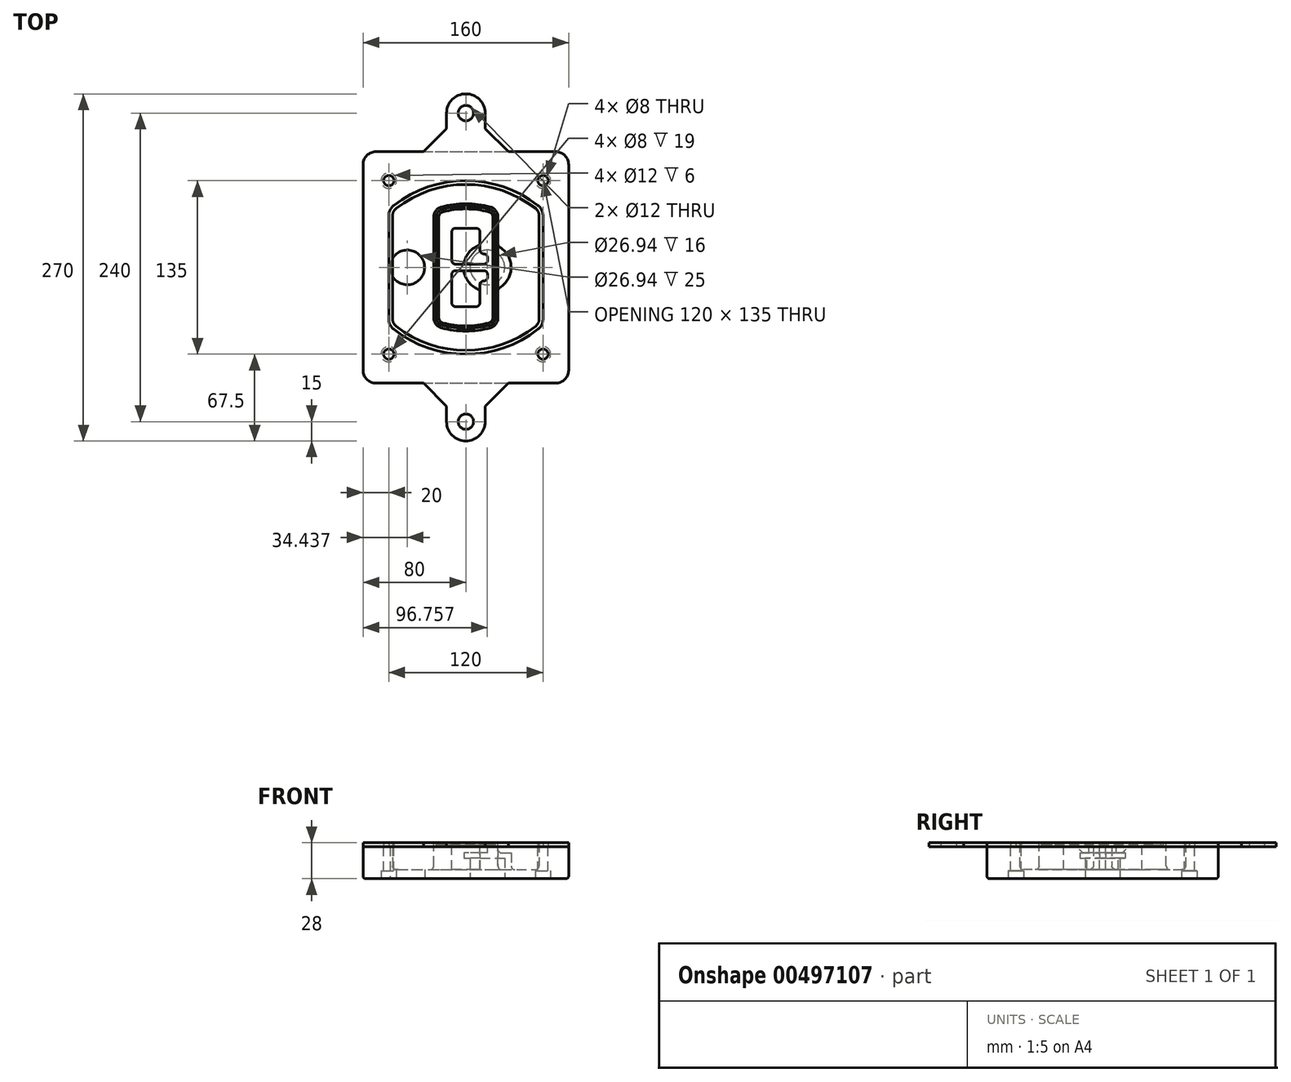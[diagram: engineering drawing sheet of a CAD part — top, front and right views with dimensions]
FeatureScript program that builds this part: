
annotation { "Feature Type Name" : "Feature", "Feature Type Description" : "" }
export const myFeature = defineFeature(function(context is Context, id is Id, definition is map)
    precondition{}
    {
        {
            var Q0;
            Q0=qCreatedBy(makeId("Top.planeOp"),FACE);
            var sketch = newSketch(context, id + "F0", { "sketchPlane" : qUnion([Q0])});
            skPoint(sketch, "E0.rect.middle", {"position": v(0, 0) * mm});
            skLineSegment(sketch, "E1.bottom", {"start": v(-70, -90) * mm, "end": v(70, -90) * mm});
            skLineSegment(sketch, "E1.top", {"start": v(-70, 90) * mm, "end": v(70, 90) * mm});
            skLineSegment(sketch, "E1.left", {"start": v(-80, -80) * mm, "end": v(-80, 80) * mm});
            skLineSegment(sketch, "E1.right", {"start": v(80, -80) * mm, "end": v(80, 80) * mm});
            skLineSegment(sketch, "E2", {"start": v(-80, 90) * mm, "end": v(80, -90) * mm, "construction": true});
            skLineSegment(sketch, "E3", {"start": v(80, 90) * mm, "end": v(-80, -90) * mm, "construction": true});
            skCircle(sketch, "E4", {"center": v(-60, 67.5) * mm, "radius": 4 * mm});
            skCircle(sketch, "E5", {"center": v(60, 67.5) * mm, "radius": 4 * mm});
            skCircle(sketch, "E6", {"center": v(60, -67.5) * mm, "radius": 4 * mm});
            skCircle(sketch, "E7", {"center": v(-60, -67.5) * mm, "radius": 4 * mm});
            skLineSegment(sketch, "E8", {"start": v(-60, 67.5) * mm, "end": v(60, 67.5) * mm, "construction": true});
            skLineSegment(sketch, "E9", {"start": v(60, 67.5) * mm, "end": v(60, -67.5) * mm, "construction": true});
            skLineSegment(sketch, "E10", {"start": v(60, -67.5) * mm, "end": v(-60, -67.5) * mm, "construction": true});
            skLineSegment(sketch, "E11", {"start": v(-60, -67.5) * mm, "end": v(-60, 67.5) * mm, "construction": true});
            skLineSegment(sketch, "E12", {"start": v(-60, 40.3) * mm, "end": v(-60, -40.3) * mm});
            skLineSegment(sketch, "E13", {"start": v(60, 40.3) * mm, "end": v(60, -40.3) * mm});
            skArc(sketch, "E14", {"start": v(56.15, 48.18) * mm, "mid": v(0, 67.5) * mm, "end": v(-56.15, 48.18) * mm});
            skArc(sketch, "E15", {"start": v(-56.15, -48.18) * mm, "mid": v(0, -67.5) * mm, "end": v(56.15, -48.18) * mm});
            skLineSegment(sketch, "E16", {"start": v(-60, 0) * mm, "end": v(60, 0) * mm, "construction": true});
            skPoint(sketch, "E17.visualSharp", {"position": v(-60, -45) * mm});
            skArc(sketch, "E17.filletArc", {"start": v(-60, -40.3) * mm, "mid": v(-58.99, -44.68) * mm, "end": v(-56.15, -48.18) * mm});
            skPoint(sketch, "E18.visualSharp", {"position": v(-60, 45) * mm});
            skArc(sketch, "E18.filletArc", {"start": v(-56.15, 48.18) * mm, "mid": v(-58.99, 44.68) * mm, "end": v(-60, 40.3) * mm});
            skPoint(sketch, "E19.visualSharp", {"position": v(60, 45) * mm});
            skArc(sketch, "E19.filletArc", {"start": v(60, 40.3) * mm, "mid": v(58.99, 44.68) * mm, "end": v(56.15, 48.18) * mm});
            skPoint(sketch, "E20.visualSharp", {"position": v(60, -45) * mm});
            skArc(sketch, "E20.filletArc", {"start": v(56.15, -48.18) * mm, "mid": v(58.99, -44.68) * mm, "end": v(60, -40.3) * mm});
            skPoint(sketch, "E21.visualSharp", {"position": v(-80, 90) * mm});
            skArc(sketch, "E21.filletArc", {"start": v(-70, 90) * mm, "mid": v(-77.07, 87.07) * mm, "end": v(-80, 80) * mm});
            skPoint(sketch, "E22.visualSharp", {"position": v(80, 90) * mm});
            skArc(sketch, "E22.filletArc", {"start": v(80, 80) * mm, "mid": v(77.07, 87.07) * mm, "end": v(70, 90) * mm});
            skPoint(sketch, "E23.visualSharp", {"position": v(80, -90) * mm});
            skArc(sketch, "E23.filletArc", {"start": v(70, -90) * mm, "mid": v(77.07, -87.07) * mm, "end": v(80, -80) * mm});
            skPoint(sketch, "E24.visualSharp", {"position": v(-80, -90) * mm});
            skArc(sketch, "E24.filletArc", {"start": v(-80, -80) * mm, "mid": v(-77.07, -87.07) * mm, "end": v(-70, -90) * mm});
            skArc(sketch, "E25.0", {"start": v(57, 40.3) * mm, "mid": v(56.3, 43.36) * mm, "end": v(54.3, 45.81) * mm});
            skLineSegment(sketch, "E25.1", {"start": v(57, 40.3) * mm, "end": v(57, -40.3) * mm});
            skArc(sketch, "E25.2", {"start": v(54.3, -45.81) * mm, "mid": v(56.3, -43.36) * mm, "end": v(57, -40.3) * mm});
            skArc(sketch, "E25.3", {"start": v(-54.3, -45.81) * mm, "mid": v(0, -64.5) * mm, "end": v(54.3, -45.81) * mm});
            skArc(sketch, "E25.4", {"start": v(-57, -40.3) * mm, "mid": v(-56.3, -43.36) * mm, "end": v(-54.3, -45.81) * mm});
            skArc(sketch, "E25.5", {"start": v(54.3, 45.81) * mm, "mid": v(0, 64.5) * mm, "end": v(-54.3, 45.81) * mm});
            skLineSegment(sketch, "E25.6", {"start": v(-57, 40.3) * mm, "end": v(-57, -40.3) * mm});
            skArc(sketch, "E25.7", {"start": v(-54.3, 45.81) * mm, "mid": v(-56.3, 43.36) * mm, "end": v(-57, 40.3) * mm});
            skArc(sketch, "E26.0", {"start": v(-58.62, 51.33) * mm, "mid": v(-62.58, 46.43) * mm, "end": v(-64, 40.3) * mm});
            skArc(sketch, "E26.1", {"start": v(58.62, 51.33) * mm, "mid": v(0, 71.5) * mm, "end": v(-58.62, 51.33) * mm});
            skArc(sketch, "E26.2", {"start": v(64, 40.3) * mm, "mid": v(62.58, 46.43) * mm, "end": v(58.62, 51.33) * mm});
            skLineSegment(sketch, "E26.3", {"start": v(64, 40.3) * mm, "end": v(64, -40.3) * mm});
            skArc(sketch, "E26.4", {"start": v(58.62, -51.33) * mm, "mid": v(62.58, -46.43) * mm, "end": v(64, -40.3) * mm});
            skLineSegment(sketch, "E26.5", {"start": v(-64, 40.3) * mm, "end": v(-64, -40.3) * mm});
            skArc(sketch, "E26.6", {"start": v(-58.62, -51.33) * mm, "mid": v(0, -71.5) * mm, "end": v(58.62, -51.33) * mm});
            skArc(sketch, "E26.7", {"start": v(-64, -40.3) * mm, "mid": v(-62.58, -46.43) * mm, "end": v(-58.62, -51.33) * mm});
            skSolve(sketch);
        }
        {
            var Q0;
            Q0=makeQuery(id+"F0.imprint","IMPRINT",FACE,{"disambiguationData":[TD([[makeQuery(id+"F0.imprint","IMPRINT",EDGE,{"derivedFrom":sQuery(id+"F0.wireOp",EDGE,"E1.bottom")}),1.0]])]});
            var Q1;
            Q1=makeQuery(id+"F0.imprint","IMPRINT",FACE,{"disambiguationData":[TD([[makeQuery(id+"F0.imprint","IMPRINT",EDGE,{"derivedFrom":sQuery(id+"F0.wireOp",EDGE,"E12")}),1.0]])]});
            var Q2;
            Q2=makeQuery(id+"F0.imprint","IMPRINT",FACE,{"disambiguationData":[TD([[makeQuery(id+"F0.imprint","IMPRINT",EDGE,{"derivedFrom":sQuery(id+"F0.wireOp",EDGE,"E25.0")}),1.0]])]});
            var Q3;
            Q3=makeQuery(id+"F0.imprint","IMPRINT",FACE,{"disambiguationData":[TD([[makeQuery(id+"F0.imprint","IMPRINT",EDGE,{"derivedFrom":sQuery(id+"F0.wireOp",EDGE,"E12")}),-1.0]])]});
            extrude(context, id + "F1", {"entities" : qUnion([Q0, Q1, Q2, Q3]), "oppositeDirection" : true, "depth" : 25 * mm});
        }
        {
            var Q0;
            Q0=makeQuery(id+"F0.imprint","IMPRINT",FACE,{"disambiguationData":[TD([[makeQuery(id+"F0.imprint","IMPRINT",EDGE,{"derivedFrom":sQuery(id+"F0.wireOp",EDGE,"E12")}),1.0]])]});
            extrude(context, id + "F2", {"entities" : qUnion([Q0]), "operationType" : NewBodyOperationType.ADD, "depth" : 3 * mm});
        }
        {
            var Q0;
            Q0=makeQuery(id+"F0.imprint","IMPRINT",FACE,{"disambiguationData":[TD([[makeQuery(id+"F0.imprint","IMPRINT",EDGE,{"derivedFrom":sQuery(id+"F0.wireOp",EDGE,"E25.0")}),1.0]])]});
            extrude(context, id + "F3", {"entities" : qUnion([Q0]), "operationType" : NewBodyOperationType.REMOVE, "oppositeDirection" : true, "depth" : 18 * mm});
        }
        {
            var Q0;
            Q0=makeQuery(id+"F2.opExtrude","CAP_FACE",FACE,{"disambiguationData":[OSD([sQuery(id+"F0.wireOp",EDGE,"E12"),sQuery(id+"F0.wireOp",EDGE,"E13"),sQuery(id+"F0.wireOp",EDGE,"E14"),sQuery(id+"F0.wireOp",EDGE,"E15"),sQuery(id+"F0.wireOp",EDGE,"E17.filletArc"),sQuery(id+"F0.wireOp",EDGE,"E18.filletArc"),sQuery(id+"F0.wireOp",EDGE,"E19.filletArc"),sQuery(id+"F0.wireOp",EDGE,"E20.filletArc"),sQuery(id+"F0.wireOp",EDGE,"E25.0"),sQuery(id+"F0.wireOp",EDGE,"E25.1"),sQuery(id+"F0.wireOp",EDGE,"E25.2"),sQuery(id+"F0.wireOp",EDGE,"E25.3"),sQuery(id+"F0.wireOp",EDGE,"E25.4"),sQuery(id+"F0.wireOp",EDGE,"E25.5"),sQuery(id+"F0.wireOp",EDGE,"E25.6"),sQuery(id+"F0.wireOp",EDGE,"E25.7")])],"isStart":false});
            var sketch = newSketch(context, id + "F4", { "sketchPlane" : qUnion([Q0])});
            skArc(sketch, "E27.0", {"start": v(-19.08, -46.97) * mm, "mid": v(0, -49.5) * mm, "end": v(19.08, -46.97) * mm});
            skArc(sketch, "E28.0", {"start": v(19.08, 46.97) * mm, "mid": v(0, 49.5) * mm, "end": v(-19.08, 46.97) * mm});
            skLineSegment(sketch, "E29", {"start": v(-25, 39.25) * mm, "end": v(-25, -39.25) * mm});
            skLineSegment(sketch, "E30", {"start": v(25, 39.25) * mm, "end": v(25, -39.25) * mm});
            skLineSegment(sketch, "E31", {"start": v(-25, 45.1) * mm, "end": v(25, 45.1) * mm, "construction": true});
            skLineSegment(sketch, "E32", {"start": v(-25, -45.1) * mm, "end": v(25, -45.1) * mm, "construction": true});
            skPoint(sketch, "E33.visualSharp", {"position": v(-25, 45.1) * mm});
            skArc(sketch, "E33.filletArc", {"start": v(-19.08, 46.97) * mm, "mid": v(-23.35, 44.11) * mm, "end": v(-25, 39.25) * mm});
            skPoint(sketch, "E34.visualSharp", {"position": v(25, 45.1) * mm});
            skArc(sketch, "E34.filletArc", {"start": v(25, 39.25) * mm, "mid": v(23.35, 44.11) * mm, "end": v(19.08, 46.97) * mm});
            skPoint(sketch, "E35.visualSharp", {"position": v(25, -45.1) * mm});
            skArc(sketch, "E35.filletArc", {"start": v(19.08, -46.97) * mm, "mid": v(23.35, -44.11) * mm, "end": v(25, -39.25) * mm});
            skPoint(sketch, "E36.visualSharp", {"position": v(-25, -45.1) * mm});
            skArc(sketch, "E36.filletArc", {"start": v(-25, -39.25) * mm, "mid": v(-23.35, -44.11) * mm, "end": v(-19.08, -46.97) * mm});
            skArc(sketch, "E37.0", {"start": v(54.3, 45.81) * mm, "mid": v(0, 64.5) * mm, "end": v(-54.3, 45.81) * mm});
            skArc(sketch, "E37.1", {"start": v(-54.3, 45.81) * mm, "mid": v(-56.3, 43.36) * mm, "end": v(-57, 40.3) * mm});
            skLineSegment(sketch, "E37.2", {"start": v(-57, 40.3) * mm, "end": v(-57, -40.3) * mm});
            skArc(sketch, "E37.3", {"start": v(-57, -40.3) * mm, "mid": v(-56.3, -43.36) * mm, "end": v(-54.3, -45.81) * mm});
            skArc(sketch, "E37.4", {"start": v(-54.3, -45.81) * mm, "mid": v(0, -64.5) * mm, "end": v(54.3, -45.81) * mm});
            skArc(sketch, "E37.5", {"start": v(54.3, -45.81) * mm, "mid": v(56.3, -43.36) * mm, "end": v(57, -40.3) * mm});
            skLineSegment(sketch, "E37.6", {"start": v(57, 40.3) * mm, "end": v(57, -40.3) * mm});
            skArc(sketch, "E37.7", {"start": v(57, 40.3) * mm, "mid": v(56.3, 43.36) * mm, "end": v(54.3, 45.81) * mm});
            skLineSegment(sketch, "E38.0", {"start": v(23, 39.25) * mm, "end": v(23, -39.25) * mm});
            skArc(sketch, "E38.1", {"start": v(18.56, -45.04) * mm, "mid": v(21.76, -42.9) * mm, "end": v(23, -39.25) * mm});
            skArc(sketch, "E38.2", {"start": v(-18.56, -45.04) * mm, "mid": v(0, -47.5) * mm, "end": v(18.56, -45.04) * mm});
            skArc(sketch, "E38.3", {"start": v(-23, -39.25) * mm, "mid": v(-21.76, -42.9) * mm, "end": v(-18.56, -45.04) * mm});
            skLineSegment(sketch, "E38.4", {"start": v(-23, 39.25) * mm, "end": v(-23, -39.25) * mm});
            skArc(sketch, "E38.5", {"start": v(23, 39.25) * mm, "mid": v(21.76, 42.9) * mm, "end": v(18.56, 45.04) * mm});
            skArc(sketch, "E38.6", {"start": v(-18.56, 45.04) * mm, "mid": v(-21.76, 42.9) * mm, "end": v(-23, 39.25) * mm});
            skArc(sketch, "E38.7", {"start": v(18.56, 45.04) * mm, "mid": v(0, 47.5) * mm, "end": v(-18.56, 45.04) * mm});
            skArc(sketch, "E39.0", {"start": v(21, 39.25) * mm, "mid": v(20.18, 41.68) * mm, "end": v(18.04, 43.1) * mm});
            skLineSegment(sketch, "E39.1", {"start": v(21, 39.25) * mm, "end": v(21, -39.25) * mm});
            skArc(sketch, "E39.2", {"start": v(18.04, -43.1) * mm, "mid": v(20.18, -41.68) * mm, "end": v(21, -39.25) * mm});
            skArc(sketch, "E39.3", {"start": v(-18.04, -43.1) * mm, "mid": v(0, -45.5) * mm, "end": v(18.04, -43.1) * mm});
            skArc(sketch, "E39.4", {"start": v(-21, -39.25) * mm, "mid": v(-20.18, -41.68) * mm, "end": v(-18.04, -43.1) * mm});
            skArc(sketch, "E39.5", {"start": v(18.04, 43.1) * mm, "mid": v(0, 45.5) * mm, "end": v(-18.04, 43.1) * mm});
            skLineSegment(sketch, "E39.6", {"start": v(-21, 39.25) * mm, "end": v(-21, -39.25) * mm});
            skArc(sketch, "E39.7", {"start": v(-18.04, 43.1) * mm, "mid": v(-20.18, 41.68) * mm, "end": v(-21, 39.25) * mm});
            skLineSegment(sketch, "E40", {"start": v(-25, 0) * mm, "end": v(25, 0) * mm, "construction": true});
            skLineSegment(sketch, "E41", {"start": v(-11, 5.5) * mm, "end": v(-11, 27.5) * mm});
            skLineSegment(sketch, "E42", {"start": v(-8, 30.5) * mm, "end": v(8, 30.5) * mm});
            skLineSegment(sketch, "E43", {"start": v(11, 27.5) * mm, "end": v(11, 13.5) * mm});
            skLineSegment(sketch, "E44", {"start": v(14, 10.5) * mm, "end": v(14, 10.5) * mm});
            skLineSegment(sketch, "E45", {"start": v(17, 7.5) * mm, "end": v(17, 5.5) * mm});
            skLineSegment(sketch, "E46", {"start": v(14, 2.5) * mm, "end": v(-8, 2.5) * mm});
            skPoint(sketch, "E47.visualSharp", {"position": v(-11, 30.5) * mm});
            skArc(sketch, "E47.filletArc", {"start": v(-8, 30.5) * mm, "mid": v(-10.12, 29.62) * mm, "end": v(-11, 27.5) * mm});
            skPoint(sketch, "E48.visualSharp", {"position": v(11, 30.5) * mm});
            skArc(sketch, "E48.filletArc", {"start": v(11, 27.5) * mm, "mid": v(10.12, 29.62) * mm, "end": v(8, 30.5) * mm});
            skPoint(sketch, "E49.visualSharp", {"position": v(11, 10.5) * mm});
            skArc(sketch, "E49.filletArc", {"start": v(11, 13.5) * mm, "mid": v(11.88, 11.38) * mm, "end": v(14, 10.5) * mm});
            skPoint(sketch, "E50.visualSharp", {"position": v(17, 10.5) * mm});
            skArc(sketch, "E50.filletArc", {"start": v(17, 7.5) * mm, "mid": v(16.12, 9.62) * mm, "end": v(14, 10.5) * mm});
            skPoint(sketch, "E51.visualSharp", {"position": v(17, 2.5) * mm});
            skArc(sketch, "E51.filletArc", {"start": v(14, 2.5) * mm, "mid": v(16.12, 3.38) * mm, "end": v(17, 5.5) * mm});
            skPoint(sketch, "E52.visualSharp", {"position": v(-11, 2.5) * mm});
            skArc(sketch, "E52.filletArc", {"start": v(-11, 5.5) * mm, "mid": v(-10.12, 3.38) * mm, "end": v(-8, 2.5) * mm});
            skLineSegment(sketch, "E53.0.MirrorCS", {"start": v(14, -2.5) * mm, "end": v(-8, -2.5) * mm});
            skArc(sketch, "E54.0.MirrorCS", {"start": v(-11, -5.5) * mm, "mid": v(-10.12, -3.38) * mm, "end": v(-8, -2.5) * mm});
            skLineSegment(sketch, "E55.0.MirrorCS", {"start": v(-11, -5.5) * mm, "end": v(-11, -27.5) * mm});
            skArc(sketch, "E56.0.MirrorCS", {"start": v(-8, -30.5) * mm, "mid": v(-10.12, -29.62) * mm, "end": v(-11, -27.5) * mm});
            skLineSegment(sketch, "E57.0.MirrorCS", {"start": v(-8, -30.5) * mm, "end": v(8, -30.5) * mm});
            skArc(sketch, "E58.0.MirrorCS", {"start": v(11, -27.5) * mm, "mid": v(10.12, -29.62) * mm, "end": v(8, -30.5) * mm});
            skLineSegment(sketch, "E59.0.MirrorCS", {"start": v(11, -27.5) * mm, "end": v(11, -13.5) * mm});
            skArc(sketch, "E60.0.MirrorCS", {"start": v(11, -13.5) * mm, "mid": v(11.88, -11.38) * mm, "end": v(14, -10.5) * mm});
            skArc(sketch, "E61.0.MirrorCS", {"start": v(17, -7.5) * mm, "mid": v(16.12, -9.62) * mm, "end": v(14, -10.5) * mm});
            skLineSegment(sketch, "E62.0.MirrorCS", {"start": v(17, -7.5) * mm, "end": v(17, -5.5) * mm});
            skArc(sketch, "E63.0.MirrorCS", {"start": v(14, -2.5) * mm, "mid": v(16.12, -3.38) * mm, "end": v(17, -5.5) * mm});
            skSolve(sketch);
        }
        {
            var Q0;
            Q0=makeQuery(id+"F4.imprint","IMPRINT",FACE,{"disambiguationData":[TD([[makeQuery(id+"F4.imprint","IMPRINT",EDGE,{"derivedFrom":sQuery(id+"F4.wireOp",EDGE,"E27.0")}),1.0]])]});
            var Q1;
            Q1=makeQuery(id+"F4.imprint","IMPRINT",FACE,{"disambiguationData":[TD([[makeQuery(id+"F4.imprint","IMPRINT",EDGE,{"derivedFrom":sQuery(id+"F4.wireOp",EDGE,"E38.0")}),-1.0]])]});
            var Q2;
            Q2=makeQuery(id+"F4.imprint","IMPRINT",FACE,{"disambiguationData":[TD([[makeQuery(id+"F4.imprint","IMPRINT",EDGE,{"derivedFrom":sQuery(id+"F4.wireOp",EDGE,"E39.0")}),1.0]])]});
            extrude(context, id + "F5", {"entities" : qUnion([Q0, Q1, Q2]), "operationType" : NewBodyOperationType.ADD, "endBound" : BoundingType.UP_TO_NEXT, "oppositeDirection" : true, "depth" : 25 * mm});
        }
        {
            var Q0;
            Q0=makeQuery(id+"F4.imprint","IMPRINT",FACE,{"disambiguationData":[TD([[makeQuery(id+"F4.imprint","IMPRINT",EDGE,{"derivedFrom":sQuery(id+"F4.wireOp",EDGE,"E38.0")}),-1.0]])]});
            extrude(context, id + "F6", {"entities" : qUnion([Q0]), "operationType" : NewBodyOperationType.REMOVE, "oppositeDirection" : true, "depth" : 2 * mm});
        }
        {
            var Q0;
            Q0=makeQuery(id+"F1.opExtrude","CAP_FACE",FACE,{"disambiguationData":[OSD([sQuery(id+"F0.wireOp",EDGE,"E1.bottom"),sQuery(id+"F0.wireOp",EDGE,"E1.top"),sQuery(id+"F0.wireOp",EDGE,"E1.left"),sQuery(id+"F0.wireOp",EDGE,"E1.right"),sQuery(id+"F0.wireOp",EDGE,"E4"),sQuery(id+"F0.wireOp",EDGE,"E5"),sQuery(id+"F0.wireOp",EDGE,"E6"),sQuery(id+"F0.wireOp",EDGE,"E7"),sQuery(id+"F0.wireOp",EDGE,"E21.filletArc"),sQuery(id+"F0.wireOp",EDGE,"E22.filletArc"),sQuery(id+"F0.wireOp",EDGE,"E23.filletArc"),sQuery(id+"F0.wireOp",EDGE,"E24.filletArc")])],"isStart":false});
            var sketch = newSketch(context, id + "F7", { "sketchPlane" : qUnion([Q0])});
            skCircle(sketch, "E64", {"center": v(16.76, 0) * mm, "radius": 13.47 * mm});
            skCircle(sketch, "E65", {"center": v(-45.56, 0) * mm, "radius": 13.47 * mm});
            skLineSegment(sketch, "E66", {"start": v(80, 0) * mm, "end": v(-80, 0) * mm});
            skCircle(sketch, "E67", {"center": v(16.76, 0) * mm, "radius": 18.47 * mm});
            skCircle(sketch, "E68", {"center": v(60, -67.5) * mm, "radius": 6 * mm});
            skCircle(sketch, "E69", {"center": v(-60, -67.5) * mm, "radius": 6 * mm});
            skCircle(sketch, "E70", {"center": v(-60, 67.5) * mm, "radius": 6 * mm});
            skCircle(sketch, "E71", {"center": v(60, 67.5) * mm, "radius": 6 * mm});
            skSolve(sketch);
        }
        {
            var Q0;
            {var subQ1=sQuery(id+"F7.wireOp",EDGE,"E66");var subQ4=sQuery(id+"F7.wireOp",EDGE,"E64");var subQ6=makeQuery(id+"F7.imprint","INTERSECT",VERTEX,{"disambiguationData":[OD(0.0)],"derivedFrom":[subQ4,subQ1]});Q0=makeQuery(id+"F7.imprint","IMPRINT",FACE,{"disambiguationData":[TD([[makeQuery(id+"F7.imprint","IMPRINT",EDGE,{"disambiguationData":[TD([[subQ6,-1.0]])],"derivedFrom":subQ4}),-1.0]])]});}
            var Q1;
            {var subQ0=sQuery(id+"F7.wireOp",EDGE,"E66");var subQ1=sQuery(id+"F7.wireOp",EDGE,"E64");var subQ3=makeQuery(id+"F7.imprint","INTERSECT",VERTEX,{"disambiguationData":[OD(0.0)],"derivedFrom":[subQ1,subQ0]});Q1=makeQuery(id+"F7.imprint","IMPRINT",FACE,{"disambiguationData":[TD([[makeQuery(id+"F7.imprint","IMPRINT",EDGE,{"disambiguationData":[TD([[subQ3,-1.0]])],"derivedFrom":subQ1}),1.0]])]});}
            var Q2;
            {var subQ0=sQuery(id+"F7.wireOp",EDGE,"E66");var subQ1=sQuery(id+"F7.wireOp",EDGE,"E64");var subQ3=makeQuery(id+"F7.imprint","INTERSECT",VERTEX,{"disambiguationData":[OD(0.0)],"derivedFrom":[subQ1,subQ0]});Q2=makeQuery(id+"F7.imprint","IMPRINT",FACE,{"disambiguationData":[TD([[makeQuery(id+"F7.imprint","IMPRINT",EDGE,{"disambiguationData":[TD([[subQ3,1.0]])],"derivedFrom":subQ1}),1.0]])]});}
            var Q3;
            {var subQ1=sQuery(id+"F7.wireOp",EDGE,"E66");var subQ4=sQuery(id+"F7.wireOp",EDGE,"E64");var subQ6=makeQuery(id+"F7.imprint","INTERSECT",VERTEX,{"disambiguationData":[OD(0.0)],"derivedFrom":[subQ4,subQ1]});Q3=makeQuery(id+"F7.imprint","IMPRINT",FACE,{"disambiguationData":[TD([[makeQuery(id+"F7.imprint","IMPRINT",EDGE,{"disambiguationData":[TD([[subQ6,1.0]])],"derivedFrom":subQ4}),-1.0]])]});}
            extrude(context, id + "F8", {"entities" : qUnion([Q0, Q1, Q2, Q3]), "operationType" : NewBodyOperationType.ADD, "oppositeDirection" : true, "depth" : 20 * mm});
        }
        {
            var Q0;
            {var subQ0=sQuery(id+"F7.wireOp",EDGE,"E66");var subQ1=sQuery(id+"F7.wireOp",EDGE,"E64");var subQ3=makeQuery(id+"F7.imprint","INTERSECT",VERTEX,{"disambiguationData":[OD(0.0)],"derivedFrom":[subQ1,subQ0]});Q0=makeQuery(id+"F7.imprint","IMPRINT",FACE,{"disambiguationData":[TD([[makeQuery(id+"F7.imprint","IMPRINT",EDGE,{"disambiguationData":[TD([[subQ3,-1.0]])],"derivedFrom":subQ1}),1.0]])]});}
            var Q1;
            {var subQ0=sQuery(id+"F7.wireOp",EDGE,"E66");var subQ1=sQuery(id+"F7.wireOp",EDGE,"E64");var subQ3=makeQuery(id+"F7.imprint","INTERSECT",VERTEX,{"disambiguationData":[OD(0.0)],"derivedFrom":[subQ1,subQ0]});Q1=makeQuery(id+"F7.imprint","IMPRINT",FACE,{"disambiguationData":[TD([[makeQuery(id+"F7.imprint","IMPRINT",EDGE,{"disambiguationData":[TD([[subQ3,1.0]])],"derivedFrom":subQ1}),1.0]])]});}
            extrude(context, id + "F9", {"entities" : qUnion([Q0, Q1]), "operationType" : NewBodyOperationType.REMOVE, "oppositeDirection" : true, "depth" : 16 * mm});
        }
        {
            var Q0;
            {var subQ0=sQuery(id+"F7.wireOp",EDGE,"E66");var subQ1=sQuery(id+"F7.wireOp",EDGE,"E65");var subQ3=makeQuery(id+"F7.imprint","INTERSECT",VERTEX,{"disambiguationData":[OD(0.0)],"derivedFrom":[subQ1,subQ0]});Q0=makeQuery(id+"F7.imprint","IMPRINT",FACE,{"disambiguationData":[TD([[makeQuery(id+"F7.imprint","IMPRINT",EDGE,{"disambiguationData":[TD([[subQ3,-1.0]])],"derivedFrom":subQ1}),1.0]])]});}
            var Q1;
            {var subQ0=sQuery(id+"F7.wireOp",EDGE,"E66");var subQ1=sQuery(id+"F7.wireOp",EDGE,"E65");var subQ3=makeQuery(id+"F7.imprint","INTERSECT",VERTEX,{"disambiguationData":[OD(0.0)],"derivedFrom":[subQ1,subQ0]});Q1=makeQuery(id+"F7.imprint","IMPRINT",FACE,{"disambiguationData":[TD([[makeQuery(id+"F7.imprint","IMPRINT",EDGE,{"disambiguationData":[TD([[subQ3,1.0]])],"derivedFrom":subQ1}),1.0]])]});}
            extrude(context, id + "F10", {"entities" : qUnion([Q0, Q1]), "operationType" : NewBodyOperationType.REMOVE, "oppositeDirection" : true, "depth" : 25 * mm});
        }
        {
            var Q0;
            Q0=makeQuery(id+"F7.imprint","IMPRINT",FACE,{"disambiguationData":[TD([[makeQuery(id+"F7.imprint","IMPRINT",EDGE,{"derivedFrom":sQuery(id+"F7.wireOp",EDGE,"E68")}),1.0]])]});
            var Q1;
            Q1=makeQuery(id+"F7.imprint","IMPRINT",FACE,{"disambiguationData":[TD([[makeQuery(id+"F7.imprint","IMPRINT",EDGE,{"derivedFrom":makeQuery(id+"F1.opExtrude","CAP_EDGE",EDGE,{"disambiguationData":[OSD([sQuery(id+"F0.wireOp",EDGE,"E5")])],"isStart":false})}),-1.0]])]});
            var Q2;
            Q2=makeQuery(id+"F7.imprint","IMPRINT",FACE,{"disambiguationData":[TD([[makeQuery(id+"F7.imprint","IMPRINT",EDGE,{"derivedFrom":sQuery(id+"F7.wireOp",EDGE,"E69")}),1.0]])]});
            var Q3;
            Q3=makeQuery(id+"F7.imprint","IMPRINT",FACE,{"disambiguationData":[TD([[makeQuery(id+"F7.imprint","IMPRINT",EDGE,{"derivedFrom":makeQuery(id+"F1.opExtrude","CAP_EDGE",EDGE,{"disambiguationData":[OSD([sQuery(id+"F0.wireOp",EDGE,"E4")])],"isStart":false})}),-1.0]])]});
            var Q4;
            Q4=makeQuery(id+"F7.imprint","IMPRINT",FACE,{"disambiguationData":[TD([[makeQuery(id+"F7.imprint","IMPRINT",EDGE,{"derivedFrom":sQuery(id+"F7.wireOp",EDGE,"E70")}),1.0]])]});
            var Q5;
            Q5=makeQuery(id+"F7.imprint","IMPRINT",FACE,{"disambiguationData":[TD([[makeQuery(id+"F7.imprint","IMPRINT",EDGE,{"derivedFrom":makeQuery(id+"F1.opExtrude","CAP_EDGE",EDGE,{"disambiguationData":[OSD([sQuery(id+"F0.wireOp",EDGE,"E7")])],"isStart":false})}),-1.0]])]});
            var Q6;
            Q6=makeQuery(id+"F7.imprint","IMPRINT",FACE,{"disambiguationData":[TD([[makeQuery(id+"F7.imprint","IMPRINT",EDGE,{"derivedFrom":sQuery(id+"F7.wireOp",EDGE,"E71")}),1.0]])]});
            var Q7;
            Q7=makeQuery(id+"F7.imprint","IMPRINT",FACE,{"disambiguationData":[TD([[makeQuery(id+"F7.imprint","IMPRINT",EDGE,{"derivedFrom":makeQuery(id+"F1.opExtrude","CAP_EDGE",EDGE,{"disambiguationData":[OSD([sQuery(id+"F0.wireOp",EDGE,"E6")])],"isStart":false})}),-1.0]])]});
            extrude(context, id + "F11", {"entities" : qUnion([Q0, Q1, Q2, Q3, Q4, Q5, Q6, Q7]), "operationType" : NewBodyOperationType.REMOVE, "oppositeDirection" : true, "depth" : 6 * mm});
        }
        {
            var Q0;
            Q0=makeQuery(id+"F9.boolean.opBoolean","COPY",FACE,{"derivedFrom":makeQuery(id+"F9.opExtrude","CAP_FACE",FACE,{"disambiguationData":[OSD([sQuery(id+"F7.wireOp",EDGE,"E64")])],"isStart":false})});
            var sketch = newSketch(context, id + "F12", { "sketchPlane" : qUnion([Q0])});
            skArc(sketch, "E72.0", {"start": v(11, 17.55) * mm, "mid": v(2.57, 11.82) * mm, "end": v(-1.54, 2.5) * mm});
            skArc(sketch, "E72.1", {"start": v(-1.54, -2.5) * mm, "mid": v(2.57, -11.82) * mm, "end": v(11, -17.55) * mm});
            skLineSegment(sketch, "E73", {"start": v(-1.54, -2.5) * mm, "end": v(14, -2.5) * mm});
            skLineSegment(sketch, "E74.0", {"start": v(14, 2.5) * mm, "end": v(-1.54, 2.5) * mm});
            skArc(sketch, "E74.1", {"start": v(14, 2.5) * mm, "mid": v(16.12, 3.38) * mm, "end": v(17, 5.5) * mm});
            skLineSegment(sketch, "E74.2", {"start": v(17, 7.5) * mm, "end": v(17, 5.5) * mm});
            skArc(sketch, "E74.3", {"start": v(17, 7.5) * mm, "mid": v(16.12, 9.62) * mm, "end": v(14, 10.5) * mm});
            skArc(sketch, "E74.4", {"start": v(11, 13.5) * mm, "mid": v(11.88, 11.38) * mm, "end": v(14, 10.5) * mm});
            skLineSegment(sketch, "E74.5", {"start": v(11, 17.55) * mm, "end": v(11, 13.5) * mm});
            skLineSegment(sketch, "E74.7", {"start": v(14, -2.5) * mm, "end": v(-1.54, -2.5) * mm});
            skArc(sketch, "E74.8", {"start": v(14, -2.5) * mm, "mid": v(16.12, -3.38) * mm, "end": v(17, -5.5) * mm});
            skLineSegment(sketch, "E74.9", {"start": v(17, -7.5) * mm, "end": v(17, -5.5) * mm});
            skArc(sketch, "E74.10", {"start": v(17, -7.5) * mm, "mid": v(16.12, -9.62) * mm, "end": v(14, -10.5) * mm});
            skArc(sketch, "E74.11", {"start": v(11, -13.5) * mm, "mid": v(11.88, -11.38) * mm, "end": v(14, -10.5) * mm});
            skLineSegment(sketch, "E74.12", {"start": v(11, -17.55) * mm, "end": v(11, -13.5) * mm});
            skPoint(sketch, "E75.orphan", {"position": v(11, -27.5) * mm});
            skPoint(sketch, "E76.orphan", {"position": v(-8, -2.5) * mm});
            skPoint(sketch, "E77.orphan", {"position": v(-8, 2.5) * mm});
            skPoint(sketch, "E78.orphan", {"position": v(11, 27.5) * mm});
            skSolve(sketch);
        }
        {
            var Q0;
            {var subQ7=sQuery(id+"F12.wireOp",EDGE,"E72.0");var subQ14=sQuery(id+"F12.wireOp",EDGE,"E72.1");var subQ16=sQuery(id+"F12.wireOp",EDGE,"E74.1");var subQ18=sQuery(id+"F12.wireOp",EDGE,"E74.8");Q0=qUnion([makeQuery(id+"F12.imprint","IMPRINT",FACE,{"disambiguationData":[TD([[makeQuery(id+"F12.imprint","IMPRINT",EDGE,{"derivedFrom":subQ7}),1.0]])]}),makeQuery(id+"F12.imprint","IMPRINT",FACE,{"disambiguationData":[TD([[makeQuery(id+"F12.imprint","IMPRINT",EDGE,{"derivedFrom":subQ14}),1.0]])]}),makeQuery(id+"F12.imprint","IMPRINT",FACE,{"disambiguationData":[TD([[makeQuery(id+"F12.imprint","IMPRINT",EDGE,{"derivedFrom":subQ16}),1.0]])]}),makeQuery(id+"F12.imprint","IMPRINT",FACE,{"disambiguationData":[TD([[makeQuery(id+"F12.imprint","IMPRINT",EDGE,{"derivedFrom":subQ18}),-1.0]])]})]);}
            var Q1;
            Q1=makeQuery(id+"F5.boolean.opBoolean","SPLIT",FACE,{"disambiguationData":[TD([makeQuery(id+"F5.opExtrude","SWEPT_FACE",FACE,{"disambiguationData":[OSD([sQuery(id+"F4.wireOp",EDGE,"E41")])]})])],"derivedFrom":makeQuery(id+"F3.boolean.opBoolean","COPY",FACE,{"derivedFrom":makeQuery(id+"F3.opExtrude","CAP_FACE",FACE,{"disambiguationData":[OSD([sQuery(id+"F0.wireOp",EDGE,"E25.0"),sQuery(id+"F0.wireOp",EDGE,"E25.1"),sQuery(id+"F0.wireOp",EDGE,"E25.2"),sQuery(id+"F0.wireOp",EDGE,"E25.3"),sQuery(id+"F0.wireOp",EDGE,"E25.4"),sQuery(id+"F0.wireOp",EDGE,"E25.5"),sQuery(id+"F0.wireOp",EDGE,"E25.6"),sQuery(id+"F0.wireOp",EDGE,"E25.7")])],"isStart":false})})});
            extrude(context, id + "F13", {"entities" : qUnion([Q0]), "operationType" : NewBodyOperationType.REMOVE, "endBound" : BoundingType.UP_TO_SURFACE, "endBoundEntityFace" : qUnion([Q1]), "depth" : 25 * mm});
        }
        {
            var Q0;
            Q0=makeQuery(id+"F3.boolean.opBoolean","COPY",EDGE,{"derivedFrom":makeQuery(id+"F3.opExtrude","CAP_EDGE",EDGE,{"disambiguationData":[OSD([sQuery(id+"F0.wireOp",EDGE,"E25.6")])],"isStart":false})});
            var Q1;
            Q1=makeQuery(id+"F8.boolean.opBoolean","INTERSECT",EDGE,{"derivedFrom":[makeQuery(id+"F5.opExtrude","SWEPT_FACE",FACE,{"disambiguationData":[OSD([sQuery(id+"F4.wireOp",EDGE,"E30")])]}),makeQuery(id+"F8.opExtrude","CAP_FACE",FACE,{"disambiguationData":[OSD([sQuery(id+"F7.wireOp",EDGE,"E67")])],"isStart":false})]});
            var Q2;
            Q2=makeQuery(id+"F8.boolean.opBoolean","INTERSECT",EDGE,{"disambiguationData":[OD(1.0)],"derivedFrom":[makeQuery(id+"F5.opExtrude","SWEPT_FACE",FACE,{"disambiguationData":[OSD([sQuery(id+"F4.wireOp",EDGE,"E30")])]}),makeQuery(id+"F8.opExtrude","SWEPT_FACE",FACE,{"disambiguationData":[OSD([sQuery(id+"F7.wireOp",EDGE,"E67")])]})]});
            var Q3;
            {var subQ0=sQuery(id+"F4.wireOp",EDGE,"E30");Q3=makeQuery(id+"F8.boolean.opBoolean","SPLIT",EDGE,{"disambiguationData":[TD([makeQuery(id+"F5.opExtrude","SWEPT_FACE",FACE,{"disambiguationData":[OSD([sQuery(id+"F4.wireOp",EDGE,"E35.filletArc")])]})])],"derivedFrom":makeQuery(id+"F5.opExtrude","CAP_EDGE",EDGE,{"disambiguationData":[OSD([subQ0])],"isStart":false})});}
            var Q4;
            {var subQ0=sQuery(id+"F0.wireOp",EDGE,"E25.7");var subQ1=sQuery(id+"F0.wireOp",EDGE,"E25.1");var subQ2=sQuery(id+"F0.wireOp",EDGE,"E25.6");var subQ3=sQuery(id+"F0.wireOp",EDGE,"E25.5");var subQ4=sQuery(id+"F0.wireOp",EDGE,"E25.4");var subQ5=sQuery(id+"F0.wireOp",EDGE,"E25.0");var subQ6=sQuery(id+"F0.wireOp",EDGE,"E25.2");var subQ7=sQuery(id+"F0.wireOp",EDGE,"E25.3");Q4=makeQuery(id+"F8.boolean.opBoolean","INTERSECT",EDGE,{"derivedFrom":[makeQuery(id+"F5.boolean.opBoolean","SPLIT",FACE,{"disambiguationData":[TD([makeQuery(id+"F2.opExtrude","SWEPT_FACE",FACE,{"disambiguationData":[OSD([subQ5])]})])],"derivedFrom":makeQuery(id+"F3.boolean.opBoolean","COPY",FACE,{"derivedFrom":makeQuery(id+"F3.opExtrude","CAP_FACE",FACE,{"disambiguationData":[OSD([subQ5,subQ1,subQ6,subQ7,subQ4,subQ3,subQ2,subQ0])],"isStart":false})})}),makeQuery(id+"F8.opExtrude","SWEPT_FACE",FACE,{"disambiguationData":[OSD([sQuery(id+"F7.wireOp",EDGE,"E67")])]})]});}
            var Q5;
            Q5=makeQuery(id+"F8.boolean.opBoolean","INTERSECT",EDGE,{"disambiguationData":[OD(0.0)],"derivedFrom":[makeQuery(id+"F5.opExtrude","SWEPT_FACE",FACE,{"disambiguationData":[OSD([sQuery(id+"F4.wireOp",EDGE,"E30")])]}),makeQuery(id+"F8.opExtrude","SWEPT_FACE",FACE,{"disambiguationData":[OSD([sQuery(id+"F7.wireOp",EDGE,"E67")])]})]});
            fillet(context, id + "F14", {"entities" : qUnion([Q0, Q1, Q2, Q3, Q4, Q5]), "radius" : 3 * mm, "tangentPropagation" : true, "allowEdgeOverflow" : false});
        }
        {
            var Q0;
            Q0=makeQuery(id+"F1.opExtrude","CAP_EDGE",EDGE,{"disambiguationData":[OSD([sQuery(id+"F0.wireOp",EDGE,"E1.bottom")])],"isStart":false});
            fillet(context, id + "F15", {"entities" : qUnion([Q0]), "radius" : 2 * mm, "tangentPropagation" : true, "allowEdgeOverflow" : false});
        }
        {
            var Q0;
            {var subQ0=sQuery(id+"F0.wireOp",EDGE,"E21.filletArc");var subQ1=sQuery(id+"F0.wireOp",EDGE,"E7");var subQ2=sQuery(id+"F0.wireOp",EDGE,"E6");var subQ3=sQuery(id+"F0.wireOp",EDGE,"E5");var subQ4=sQuery(id+"F0.wireOp",EDGE,"E4");var subQ5=sQuery(id+"F0.wireOp",EDGE,"E22.filletArc");var subQ6=sQuery(id+"F0.wireOp",EDGE,"E1.bottom");var subQ7=sQuery(id+"F0.wireOp",EDGE,"E1.right");var subQ8=sQuery(id+"F0.wireOp",EDGE,"E1.top");var subQ9=sQuery(id+"F0.wireOp",EDGE,"E1.left");var subQ10=sQuery(id+"F0.wireOp",EDGE,"E23.filletArc");var subQ11=sQuery(id+"F0.wireOp",EDGE,"E24.filletArc");Q0=makeQuery(id+"F2.boolean.opBoolean","SPLIT",FACE,{"disambiguationData":[TD([makeQuery(id+"F1.opExtrude","SWEPT_FACE",FACE,{"disambiguationData":[OSD([subQ6])]})])],"derivedFrom":makeQuery(id+"F1.opExtrude","CAP_FACE",FACE,{"disambiguationData":[OSD([subQ6,subQ8,subQ9,subQ7,subQ4,subQ3,subQ2,subQ1,subQ0,subQ5,subQ10,subQ11])],"isStart":true})});}
            var sketch = newSketch(context, id + "F16", { "sketchPlane" : qUnion([Q0])});
            skArc(sketch, "E79.0", {"start": v(-70, 90) * mm, "mid": v(-77.07, 87.07) * mm, "end": v(-80, 80) * mm});
            skLineSegment(sketch, "E80.0", {"start": v(-80, -80) * mm, "end": v(-80, 80) * mm});
            skLineSegment(sketch, "E81.0", {"start": v(-70, 90) * mm, "end": v(70, 90) * mm});
            skArc(sketch, "E82.0", {"start": v(80, 80) * mm, "mid": v(77.07, 87.07) * mm, "end": v(70, 90) * mm});
            skLineSegment(sketch, "E83.0", {"start": v(80, -80) * mm, "end": v(80, 80) * mm});
            skArc(sketch, "E84.0", {"start": v(70, -90) * mm, "mid": v(77.07, -87.07) * mm, "end": v(80, -80) * mm});
            skLineSegment(sketch, "E85.0", {"start": v(-70, -90) * mm, "end": v(70, -90) * mm});
            skArc(sketch, "E86.0", {"start": v(-80, -80) * mm, "mid": v(-77.07, -87.07) * mm, "end": v(-70, -90) * mm});
            skCircle(sketch, "E87.0", {"center": v(-60, -67.5) * mm, "radius": 4 * mm});
            skCircle(sketch, "E88.0", {"center": v(-60, 67.5) * mm, "radius": 4 * mm});
            skCircle(sketch, "E89.0", {"center": v(60, 67.5) * mm, "radius": 4 * mm});
            skCircle(sketch, "E90.0", {"center": v(60, -67.5) * mm, "radius": 4 * mm});
            skLineSegment(sketch, "E91.0", {"start": v(-60, 40.3) * mm, "end": v(-60, -40.3) * mm});
            skArc(sketch, "E92.0", {"start": v(56.15, 48.18) * mm, "mid": v(0, 67.5) * mm, "end": v(-56.15, 48.18) * mm});
            skArc(sketch, "E93.0", {"start": v(-56.15, 48.18) * mm, "mid": v(-58.99, 44.68) * mm, "end": v(-60, 40.3) * mm});
            skArc(sketch, "E94.0", {"start": v(60, 40.3) * mm, "mid": v(58.99, 44.68) * mm, "end": v(56.15, 48.18) * mm});
            skLineSegment(sketch, "E95.0", {"start": v(60, 40.3) * mm, "end": v(60, -40.3) * mm});
            skArc(sketch, "E96.0", {"start": v(56.15, -48.18) * mm, "mid": v(58.99, -44.68) * mm, "end": v(60, -40.3) * mm});
            skArc(sketch, "E97.0", {"start": v(-56.15, -48.18) * mm, "mid": v(0, -67.5) * mm, "end": v(56.15, -48.18) * mm});
            skArc(sketch, "E98.0", {"start": v(-60, -40.3) * mm, "mid": v(-58.99, -44.68) * mm, "end": v(-56.15, -48.18) * mm});
            skLineSegment(sketch, "E99", {"start": v(-33, 90) * mm, "end": v(-15, 108) * mm});
            skLineSegment(sketch, "E100", {"start": v(33, 90) * mm, "end": v(15, 108) * mm});
            skLineSegment(sketch, "E101", {"start": v(-15, 108) * mm, "end": v(-15, 120) * mm});
            skLineSegment(sketch, "E102", {"start": v(15, 108) * mm, "end": v(15, 120) * mm});
            skLineSegment(sketch, "E103", {"start": v(0, 90) * mm, "end": v(0, 120) * mm, "construction": true});
            skCircle(sketch, "E104", {"center": v(0, 120) * mm, "radius": 6 * mm});
            skArc(sketch, "E105", {"start": v(15, 120) * mm, "mid": v(0, 135) * mm, "end": v(-15, 120) * mm});
            skLineSegment(sketch, "E106", {"start": v(-15, 108) * mm, "end": v(-15, 90) * mm, "construction": true});
            skLineSegment(sketch, "E107", {"start": v(-80, 0) * mm, "end": v(80, 0) * mm, "construction": true});
            skLineSegment(sketch, "E108.MirrorCS", {"start": v(-15, -108) * mm, "end": v(-15, -120) * mm});
            skArc(sketch, "E109.MirrorCS", {"start": v(15, -120) * mm, "mid": v(0, -135) * mm, "end": v(-15, -120) * mm});
            skLineSegment(sketch, "E110.MirrorCS", {"start": v(15, -108) * mm, "end": v(15, -120) * mm});
            skCircle(sketch, "E111.MirrorC", {"center": v(0, -120) * mm, "radius": 6 * mm});
            skLineSegment(sketch, "E112.MirrorCS", {"start": v(-33, -90) * mm, "end": v(-15, -108) * mm});
            skLineSegment(sketch, "E113.MirrorCS", {"start": v(33, -90) * mm, "end": v(15, -108) * mm});
            skLineSegment(sketch, "E114.MirrorCS", {"start": v(0, -90) * mm, "end": v(0, -120) * mm, "construction": true});
            skSolve(sketch);
        }
        {
            var Q0;
            Q0 = qSketchRegion(id + "F16", true);
            var Q1;
            Q1=makeQuery(id+"F2.opExtrude","CAP_FACE",FACE,{"disambiguationData":[OSD([sQuery(id+"F0.wireOp",EDGE,"E12"),sQuery(id+"F0.wireOp",EDGE,"E13"),sQuery(id+"F0.wireOp",EDGE,"E14"),sQuery(id+"F0.wireOp",EDGE,"E15"),sQuery(id+"F0.wireOp",EDGE,"E17.filletArc"),sQuery(id+"F0.wireOp",EDGE,"E18.filletArc"),sQuery(id+"F0.wireOp",EDGE,"E19.filletArc"),sQuery(id+"F0.wireOp",EDGE,"E20.filletArc"),sQuery(id+"F0.wireOp",EDGE,"E25.0"),sQuery(id+"F0.wireOp",EDGE,"E25.1"),sQuery(id+"F0.wireOp",EDGE,"E25.2"),sQuery(id+"F0.wireOp",EDGE,"E25.3"),sQuery(id+"F0.wireOp",EDGE,"E25.4"),sQuery(id+"F0.wireOp",EDGE,"E25.5"),sQuery(id+"F0.wireOp",EDGE,"E25.6"),sQuery(id+"F0.wireOp",EDGE,"E25.7")])],"isStart":false});
            extrude(context, id + "F17", {"entities" : qUnion([Q0]), "endBound" : BoundingType.UP_TO_SURFACE, "endBoundEntityFace" : qUnion([Q1]), "depth" : 25 * mm});
        }
    });
